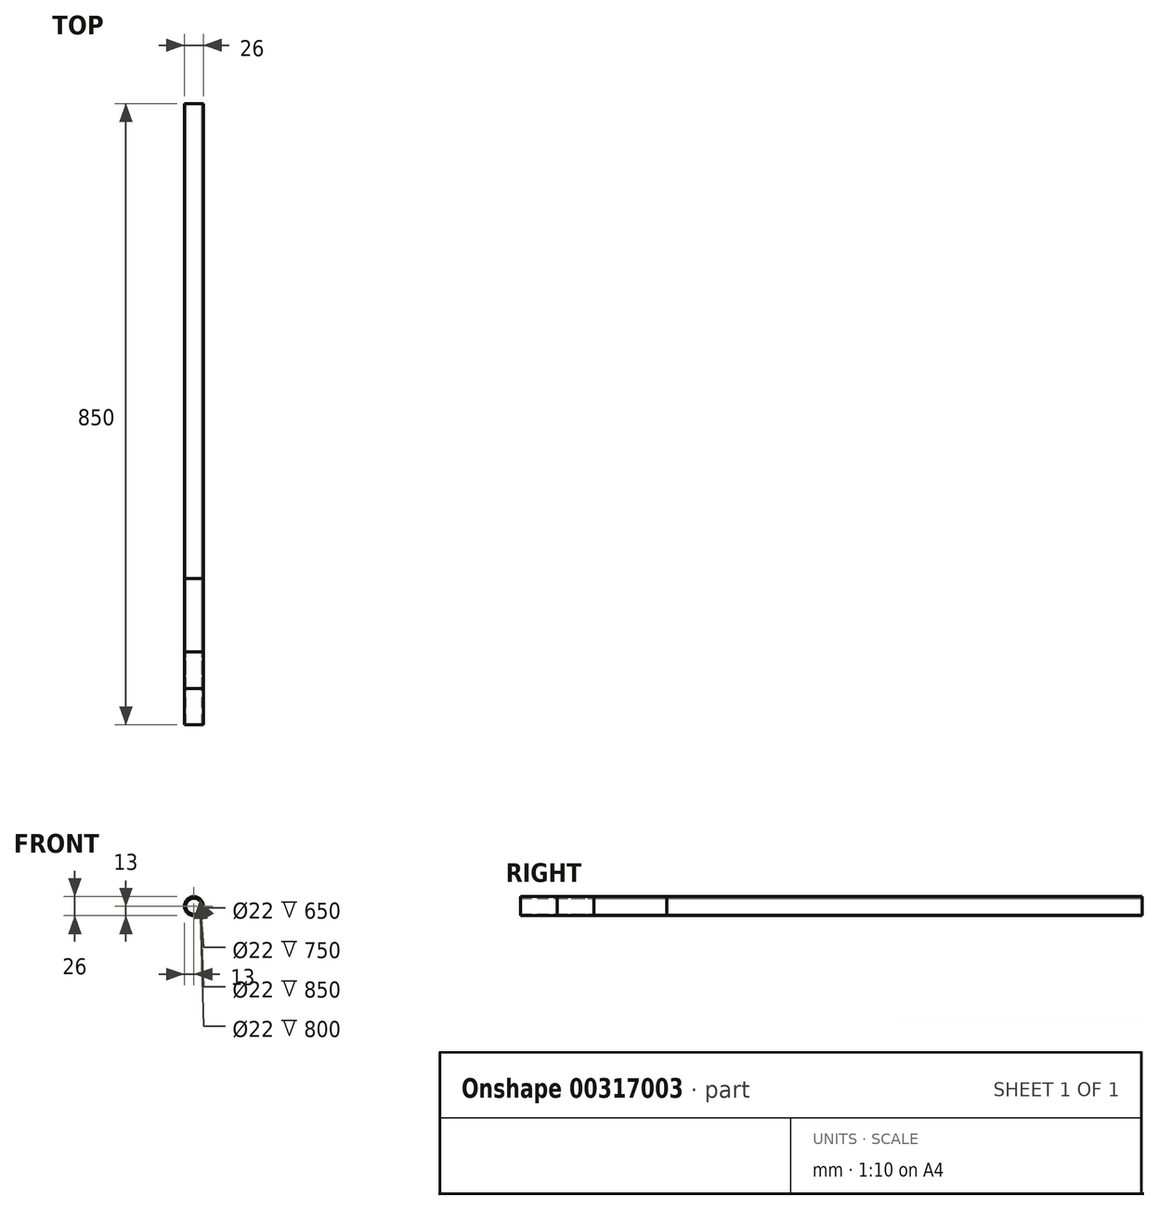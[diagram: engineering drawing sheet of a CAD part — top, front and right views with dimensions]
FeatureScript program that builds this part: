
annotation { "Feature Type Name" : "Feature", "Feature Type Description" : "" }
export const myFeature = defineFeature(function(context is Context, id is Id, definition is map)
    precondition{}
    {
        {
            var Q0;
            Q0=qCreatedBy(makeId("Front.planeOp"),FACE);
            var sketch = newSketch(context, id + "F0", { "sketchPlane" : qUnion([Q0])});
            skCircle(sketch, "E0", {"center": v(0, 0) * mm, "radius": 13 * mm});
            skCircle(sketch, "E1", {"center": v(0, 0) * mm, "radius": 11 * mm});
            skSolve(sketch);
        }
        {
            var Q0;
            Q0=makeQuery(id+"F0.imprint","IMPRINT",FACE,{"disambiguationData":[TD([[makeQuery(id+"F0.imprint","IMPRINT",EDGE,{"derivedFrom":sQuery(id+"F0.wireOp",EDGE,"E0")}),1.0]])]});
            extrude(context, id + "F1", {"entities" : qUnion([Q0]), "depth" : 800 * mm});
        }
        {
            var Q0;
            Q0=makeQuery(id+"F0.imprint","IMPRINT",FACE,{"disambiguationData":[TD([[makeQuery(id+"F0.imprint","IMPRINT",EDGE,{"derivedFrom":sQuery(id+"F0.wireOp",EDGE,"E0")}),1.0]])]});
            extrude(context, id + "F2", {"entities" : qUnion([Q0]), "depth" : 750 * mm});
        }
        {
            var Q0;
            Q0 = qSketchRegion(id + "F0", true);
            extrude(context, id + "F3", {"entities" : qUnion([Q0]), "depth" : 850 * mm});
        }
        {
            var Q0;
            Q0 = qSketchRegion(id + "F0", true);
            extrude(context, id + "F4", {"entities" : qUnion([Q0]), "depth" : 650 * mm});
        }
    });
